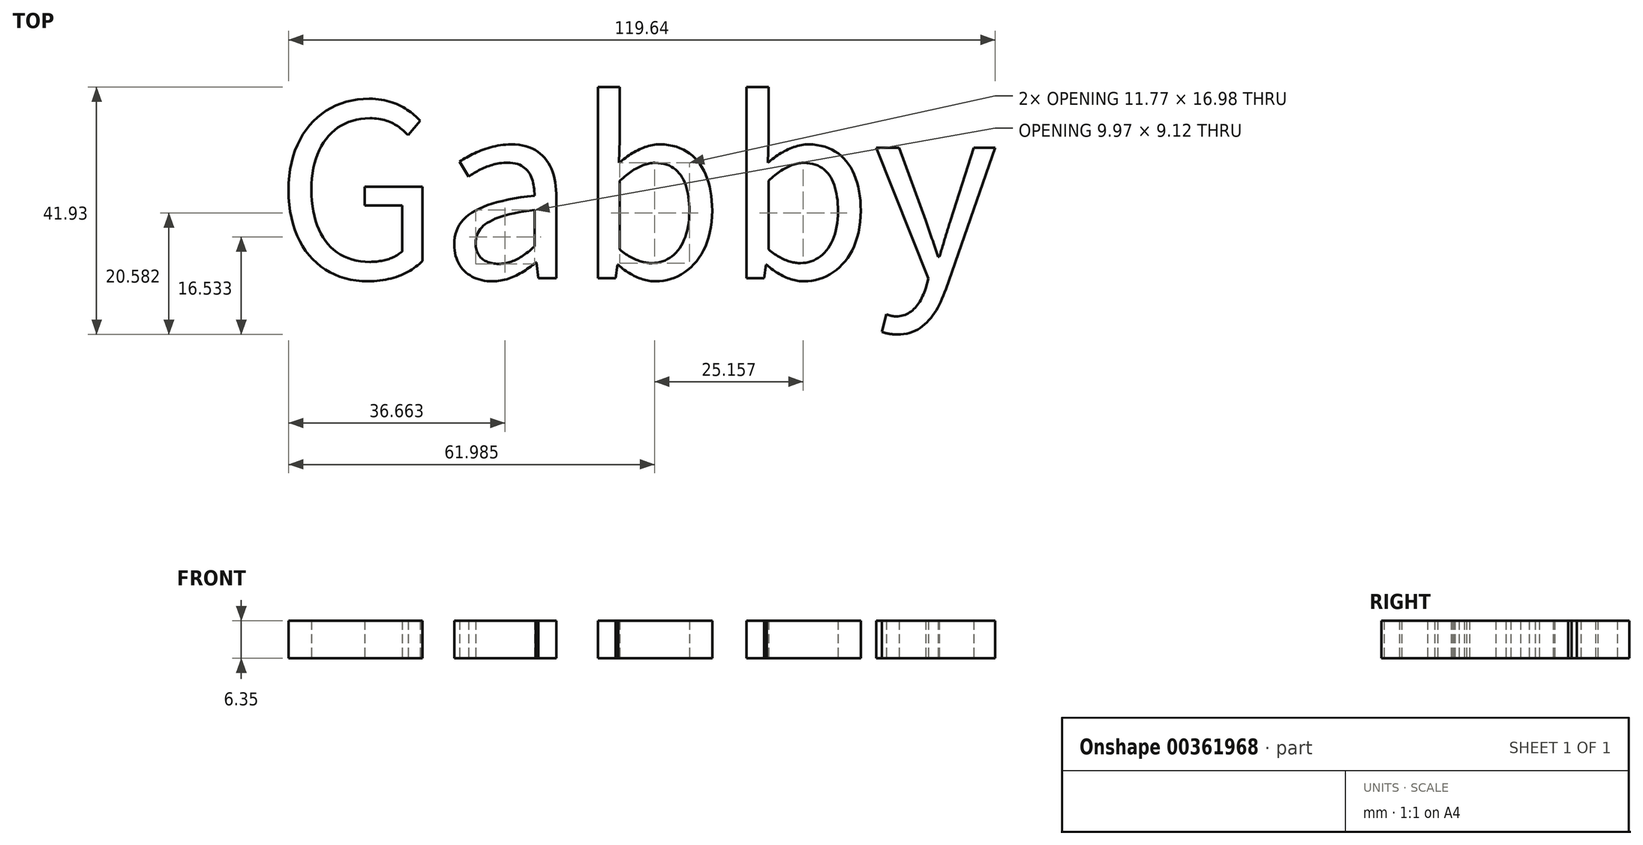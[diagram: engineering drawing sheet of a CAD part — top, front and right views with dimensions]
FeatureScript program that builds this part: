
annotation { "Feature Type Name" : "Feature", "Feature Type Description" : "" }
export const myFeature = defineFeature(function(context is Context, id is Id, definition is map)
    precondition{}
    {
        {
            var Q0;
            Q0=qCreatedBy(makeId("Top.planeOp"),FACE);
            var sketch = newSketch(context, id + "F0", { "sketchPlane" : qUnion([Q0])});
            skText(sketch, "E0", { "text": "Gabby", "fontName": "NotoSansCJKjp-Regular.otf"});
            skLineSegment(sketch, "E1", {"start": v(-5.5, 15.6) * mm, "end": v(-5.5, -16.5) * mm, "construction": true});
            const initialGuessF0  = {"E0": [-0.05993, -0.01707, 1, 0, 0.02931]};
            skSetInitialGuess(sketch, initialGuessF0);
            skSolve(sketch);
        }
        {
            var Q0;
            Q0 = qSketchRegion(id + "F0", true);
            extrude(context, id + "F1", {"entities" : qUnion([Q0]), "depth" : 6.35 * mm});
        }
    });
